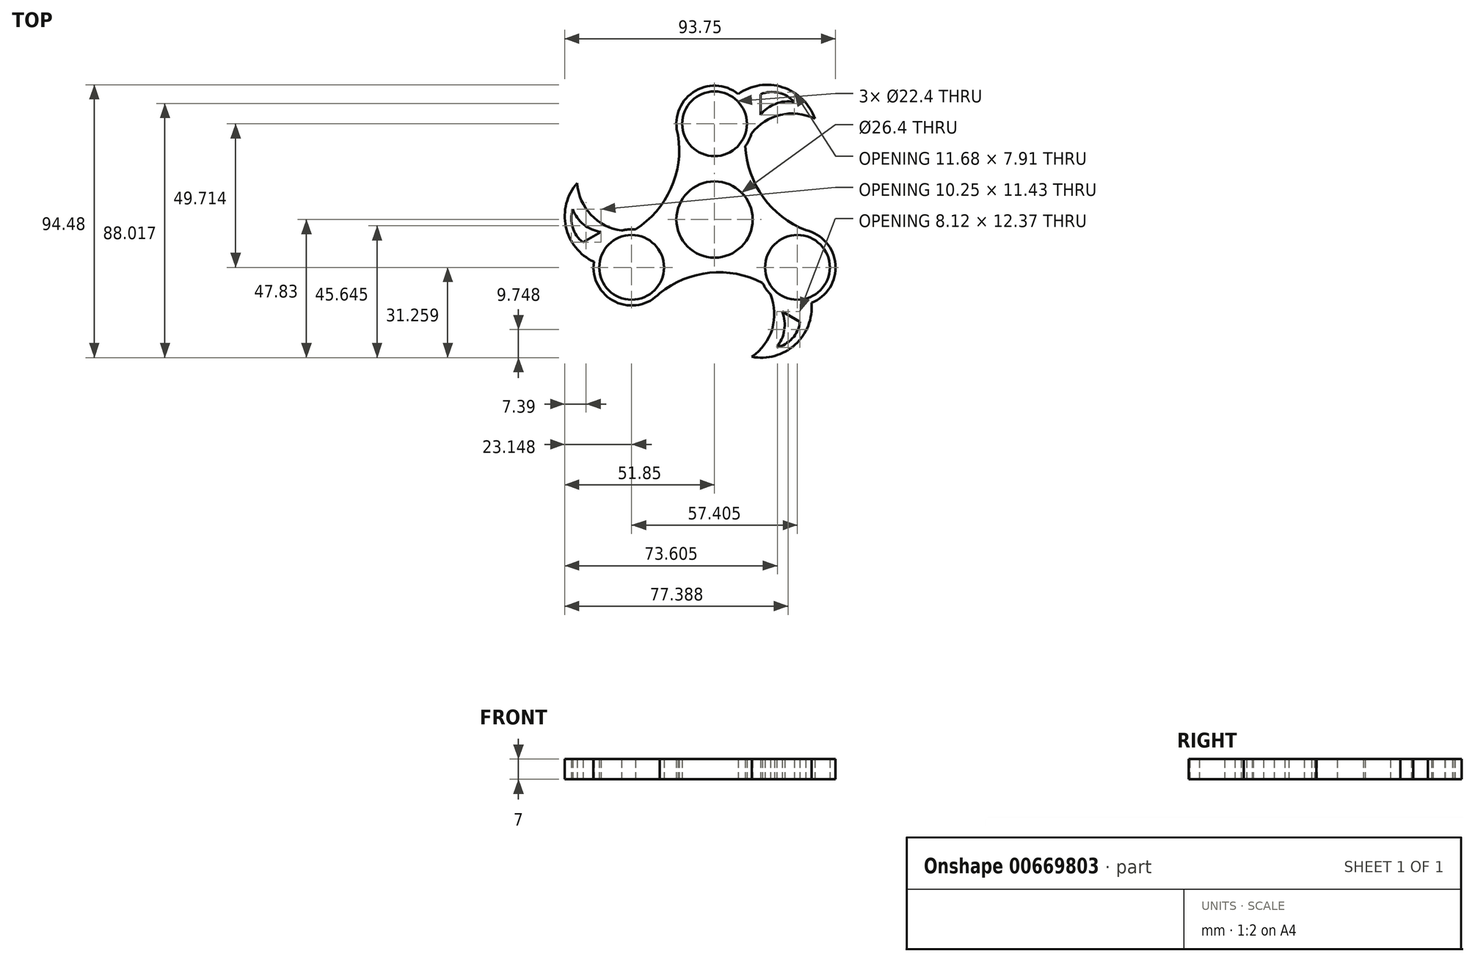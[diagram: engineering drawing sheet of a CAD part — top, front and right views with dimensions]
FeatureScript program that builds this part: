
annotation { "Feature Type Name" : "Feature", "Feature Type Description" : "" }
export const myFeature = defineFeature(function(context is Context, id is Id, definition is map)
    precondition{}
    {
        {
            var Q0;
            Q0=qCreatedBy(makeId("Top.planeOp"),FACE);
            var sketch = newSketch(context, id + "F0", { "sketchPlane" : qUnion([Q0])});
            skCircle(sketch, "E0", {"center": v(0, 0) * mm, "radius": 11.2 * mm});
            skCircle(sketch, "E1", {"center": v(0, 0) * mm, "radius": 13.2 * mm});
            skCircle(sketch, "E2", {"center": v(0, 33.14) * mm, "radius": 11.2 * mm});
            skCircle(sketch, "E3", {"center": v(0, 33.14) * mm, "radius": 13.2 * mm});
            skCircle(sketch, "E4.1.0", {"center": v(-28.7, -16.57) * mm, "radius": 13.2 * mm});
            skCircle(sketch, "E4.1.1", {"center": v(-28.7, -16.57) * mm, "radius": 11.2 * mm});
            skCircle(sketch, "E4.2.0", {"center": v(28.7, -16.57) * mm, "radius": 13.2 * mm});
            skCircle(sketch, "E4.2.1", {"center": v(28.7, -16.57) * mm, "radius": 11.2 * mm});
            skArc(sketch, "E5", {"start": v(-27.33, -3.44) * mm, "mid": v(-15.12, 10.7) * mm, "end": v(-12.6, 29.2) * mm});
            skArc(sketch, "E6.1.0", {"start": v(16.65, -21.95) * mm, "mid": v(-1.7, -18.44) * mm, "end": v(-19, -25.52) * mm});
            skArc(sketch, "E6.2.0", {"start": v(10.68, 25.4) * mm, "mid": v(16.82, 7.74) * mm, "end": v(31.6, -3.7) * mm});
            skArc(sketch, "E7", {"start": v(34.72, 34.9) * mm, "mid": v(23.6, 45.8) * mm, "end": v(8.2, 43.49) * mm});
            skArc(sketch, "E8", {"start": v(34.72, 34.9) * mm, "mid": v(22.84, 36.23) * mm, "end": v(12.77, 29.79) * mm});
            skLineSegment(sketch, "E9", {"start": v(15.91, 43.36) * mm, "end": v(15.91, 36.23) * mm});
            skPoint(sketch, "E9.endSnap0", {"position": v(22.84, 36.23) * mm});
            skArc(sketch, "E10", {"start": v(27.6, 40.74) * mm, "mid": v(22.17, 43.91) * mm, "end": v(15.91, 43.36) * mm});
            skArc(sketch, "E11", {"start": v(27.6, 40.74) * mm, "mid": v(21.14, 40.09) * mm, "end": v(15.91, 36.23) * mm});
            skArc(sketch, "E12.1.0", {"start": v(-47.58, 12.62) * mm, "mid": v(-51.47, -2.46) * mm, "end": v(-41.76, -14.65) * mm});
            skArc(sketch, "E12.1.1", {"start": v(-47.58, 12.62) * mm, "mid": v(-42.8, 1.66) * mm, "end": v(-32.18, -3.84) * mm});
            skArc(sketch, "E12.1.2", {"start": v(-49.07, 3.53) * mm, "mid": v(-45.28, -1.74) * mm, "end": v(-39.33, -4.33) * mm});
            skArc(sketch, "E12.1.3", {"start": v(-49.07, 3.53) * mm, "mid": v(-49.12, -2.75) * mm, "end": v(-45.51, -7.9) * mm});
            skLineSegment(sketch, "E12.1.4", {"start": v(-45.51, -7.9) * mm, "end": v(-39.33, -4.33) * mm});
            skArc(sketch, "E12.2.0", {"start": v(12.86, -47.52) * mm, "mid": v(27.87, -43.34) * mm, "end": v(33.56, -28.84) * mm});
            skArc(sketch, "E12.2.1", {"start": v(12.86, -47.52) * mm, "mid": v(19.96, -37.9) * mm, "end": v(19.41, -25.95) * mm});
            skArc(sketch, "E12.2.2", {"start": v(21.48, -44.27) * mm, "mid": v(24.15, -38.35) * mm, "end": v(23.42, -31.9) * mm});
            skArc(sketch, "E12.2.3", {"start": v(21.48, -44.27) * mm, "mid": v(26.94, -41.16) * mm, "end": v(29.6, -35.46) * mm});
            skLineSegment(sketch, "E12.2.4", {"start": v(29.6, -35.46) * mm, "end": v(23.42, -31.9) * mm});
            skArc(sketch, "E13", {"start": v(-12.6, 29.2) * mm, "mid": v(-24.08, 14.74) * mm, "end": v(-27.33, -3.44) * mm});
            skArc(sketch, "E14", {"start": v(-27.33, -3.44) * mm, "mid": v(-18.5, 12.22) * mm, "end": v(-12.6, 29.2) * mm});
            skArc(sketch, "E15.1.0", {"start": v(16.65, -21.95) * mm, "mid": v(-1.33, -22.13) * mm, "end": v(-19, -25.52) * mm});
            skArc(sketch, "E15.1.1", {"start": v(-19, -25.52) * mm, "mid": v(-0.72, -28.22) * mm, "end": v(16.65, -21.95) * mm});
            skArc(sketch, "E15.2.0", {"start": v(10.68, 25.4) * mm, "mid": v(19.83, 9.9) * mm, "end": v(31.6, -3.7) * mm});
            skArc(sketch, "E15.2.1", {"start": v(31.6, -3.7) * mm, "mid": v(24.8, 13.48) * mm, "end": v(10.68, 25.4) * mm});
            skSolve(sketch);
        }
        {
            var Q0;
            {var subQ0=sQuery(id+"F0.wireOp",EDGE,"E7");Q0=makeQuery(id+"F0.imprint","IMPRINT",FACE,{"disambiguationData":[TD([[makeQuery(id+"F0.imprint","IMPRINT",EDGE,{"derivedFrom":subQ0}),1.0]])]});}
            var Q1;
            Q1=makeQuery(id+"F0.imprint","IMPRINT",FACE,{"disambiguationData":[TD([[makeQuery(id+"F0.imprint","IMPRINT",EDGE,{"derivedFrom":sQuery(id+"F0.wireOp",EDGE,"E2")}),-1.0]])]});
            var Q2;
            Q2=makeQuery(id+"F0.imprint","IMPRINT",FACE,{"disambiguationData":[TD([[makeQuery(id+"F0.imprint","IMPRINT",EDGE,{"derivedFrom":sQuery(id+"F0.wireOp",EDGE,"E4.2.1")}),-1.0]])]});
            var Q3;
            Q3=makeQuery(id+"F0.imprint","IMPRINT",FACE,{"disambiguationData":[TD([[makeQuery(id+"F0.imprint","IMPRINT",EDGE,{"derivedFrom":sQuery(id+"F0.wireOp",EDGE,"E1")}),-1.0]])]});
            var Q4;
            {var subQ1=sQuery(id+"F0.wireOp",EDGE,"E12.2.0");Q4=makeQuery(id+"F0.imprint","IMPRINT",FACE,{"disambiguationData":[TD([[makeQuery(id+"F0.imprint","IMPRINT",EDGE,{"derivedFrom":subQ1}),1.0]])]});}
            var Q5;
            Q5=makeQuery(id+"F0.imprint","IMPRINT",FACE,{"disambiguationData":[TD([[makeQuery(id+"F0.imprint","IMPRINT",EDGE,{"derivedFrom":sQuery(id+"F0.wireOp",EDGE,"E4.1.1")}),-1.0]])]});
            var Q6;
            {var subQ1=sQuery(id+"F0.wireOp",EDGE,"E12.1.0");Q6=makeQuery(id+"F0.imprint","IMPRINT",FACE,{"disambiguationData":[TD([[makeQuery(id+"F0.imprint","IMPRINT",EDGE,{"derivedFrom":subQ1}),1.0]])]});}
            extrude(context, id + "F1", {"entities" : qUnion([Q0, Q1, Q2, Q3, Q4, Q5, Q6]), "depth" : 7 * mm, "offsetDistance" : 25 * mm});
        }
    });
